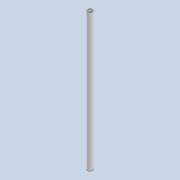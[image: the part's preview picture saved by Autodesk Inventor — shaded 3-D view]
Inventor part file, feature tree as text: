
AUTODESK INVENTOR PART (.ipt)
format: ipt  version: 2020 (Build 240168000, 168)  size: 72,192 bytes
history: native  units: mm
features: extrude x1, sketch x1
ambient origin geometry x8: Origin, YZ Plane, XZ Plane, XY Plane, X Axis, Y Axis, Z Axis, Center Point
bodies: Solid1 (feature_tree)
feature tree (2):
  extrude  "Extrusion1"  Depth=70.0mm
  sketch  "Sketch1"  dims[d0=2.5mm d1=1.8mm d2=70.0mm d3=0.0mm]
